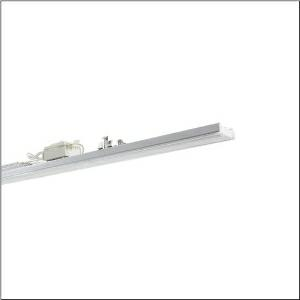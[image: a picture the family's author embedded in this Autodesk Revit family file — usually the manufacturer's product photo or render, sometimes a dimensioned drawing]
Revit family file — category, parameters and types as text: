
# Revit family: licross_r__21_recessed_mo_52tl10mn6axg_57fe
name_source: partatom
category: Lighting Fixtures
units: mm (PartAtom-declared; Revit-internal decimal feet)

## family parameters
Cut with Voids When Loaded = No
Host = Face
Light Source = No
Part Type = Normal
Room Calculation Point = No
Round Connector Dimension = Use Diameter
Shared = No

## types (1)
- --- (1 x LED, 10400 lm, 60.5 W, 6500K)
    Apparent Load = 61 VA
    CIE Flux Codes = 50 81 96 100 100
    Color Rendering = 80
    Color Temperature = 6500K
    Default Elevation = 1800 mm
    Description = Licross® 21 Recessed MO, luminaire insert, of sheet steel, galvanised, coil coated, white, length: 1.500mm, width: 66mm, height: 67mm, LED rated luminous flux: 10.400lm, light colour: 865, control gear: ON/OFF Multilumen, with plug, 3-pole, with phase selection, mains connection: 220..240V, AC, 50/60Hz, rated input power: 61W, internal wiring halogen-free, primary optical cover: cover, of PMMA, light emission: direct distribution, primary light characteristic: symmetric, protection rating (complete): IP40, insulation class (complete): insulation class I (protective earthing), certification: CE, ENEC, VDE, UKCA, protection symbol: D if used in an environment without relevant dust loads with corresponding accessories, impact resistance: IK06, permissible ambient temperature for indoor applications: -35..+40°C, corresponds to IFS (International Featured Standards) requirements for safety and quality in the food industry, reducing of maximum allowable ambient temperature of 5°C with ceiling mounting, LABS conformity tested according to VDMA 24364:2018-05, packaging unit: 1 piece
    Height = 58 mm
    Lamp = 1 x LED
    Lamp Light Flux = 10400 lm
    Lamp Power = 60.5 W
    Lamp count = 1
    Length = 1500 mm
    Luminous efficacy = 172 lm/W
    Manufacturer = Siteco
    ModVariant = No
    Model = 52TL10MN6AXG
    Mounting Place = Ceiling
    Mounting Type = Pendant
    Number of Poles = 1
    OnlyDefault = Yes
    Power Factor = 1
    Product Name = Licross® 21 Recessed MO
    Product group = luminaire insert | ceiling pendant
    ProductGroupID = 902
    Protection Class = Protection class I
    Protection Degree = IP 40
    RLX_Detail_Level = 1
    RLX_Emergency_Light_Flux = 0 lm
    RLX_Emergency_Type = 0
    RLX_Emergency_Type_DB = No
    RlxData = <blob elided: 22105 chars, md5=89e84349>
    Socket = socket
    Standby Power = 0 W
    System Light Flux = 10400 lm
    System Power = 61 W
    Type Comments = factory setting: luminous flux: 100 % | (A | C | E) | 140 mA
    Type Image = l_1296930.jpg
    URL = http://relux.com
    VarID = @adj_069579
    Voltage = 0 V
    Weight = 0.00 kg
    Width = 66 mm

## geometry (parser evidence)
native form markers: Blend x4, Sweep x11
no freeform markers — native parametric forms only
